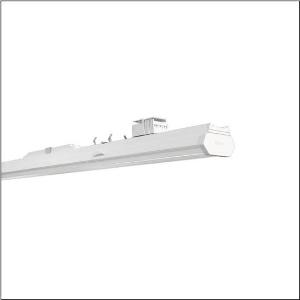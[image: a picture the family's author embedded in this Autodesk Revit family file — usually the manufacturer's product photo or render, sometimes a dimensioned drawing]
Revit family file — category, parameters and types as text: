
# Revit family: licross_r__21_protected_ho_52td13mn4fxs_5700
name_source: partatom
category: Lighting Fixtures
units: mm (PartAtom-declared; Revit-internal decimal feet)

## family parameters
Cut with Voids When Loaded = No
Host = Face
Light Source = No
Part Type = Normal
Room Calculation Point = No
Round Connector Dimension = Use Diameter
Shared = No

## types (1)
- --- (1 x LED, 15060 lm, 83.2 W, 4000K)
    Apparent Load = 83 VA
    CIE Flux Codes = 89 96 99 100 99
    Color Rendering = 80
    Color Temperature = 4000K
    Default Elevation = 1800 mm
    Description = Licross® 21 Protected HO, luminaire insert, of sheet steel, galvanised, coil coated, white, length: 1.500mm, width: 66mm, height: 67mm, LED rated luminous flux: 15.060lm, light colour: 840, control gear: ON/OFF Multilumen, with plug, 3-pole, with phase selection, mains connection: 220..240V, AC, 50/60Hz, rated input power: 83W, halogen-free wiring, primary light control with lens, of plastic, primary optical cover: cover, of PMMA, light emission: direct distribution, primary light characteristic: symmetric, protection rating (complete): IP54, insulation class (complete): insulation class I (protective earthing), certification: CE, ENEC, VDE, UKCA, protection symbol: D if used in an environment with non-conductive dust loads with corresponding accessories, impact resistance: IK06, permissible ambient temperature for indoor applications: -35..+35°C, corresponds to IFS (International Featured Standards) requirements for safety and quality in the food industry, reducing of maximum allowable ambient temperature of 5°C with ceiling mounting, LABS conformity tested according to VDMA 24364:2018-05, packaging unit: 1 piece
    Height = 92 mm
    Lamp = 1 x LED
    Lamp Light Flux = 15060 lm
    Lamp Power = 83.2 W
    Lamp count = 1
    Length = 1500 mm
    Luminous efficacy = 181 lm/W
    Manufacturer = Siteco
    ModVariant = No
    Model = 52TD13MN4FXS
    Mounting Place = Ceiling
    Mounting Type = Pendant
    Number of Poles = 1
    OnlyDefault = Yes
    Power Factor = 1
    Product Name = Licross® 21 Protected HO
    Product group = luminaire insert
    ProductGroupID = 901
    Protection Class = Protection class I
    Protection Degree = IP 54
    RLX_Detail_Level = 1
    RLX_Emergency_Light_Flux = 0 lm
    RLX_Emergency_Type = 0
    RLX_Emergency_Type_DB = No
    RlxData = <blob elided: 21993 chars, md5=baf12fe6>
    Socket = socket
    Standby Power = 0 W
    System Light Flux = 15060 lm
    System Power = 83 W
    Type Comments = factory setting: luminous flux: 100 % | (A | C | E) | 195 mA
    Type Image = l_1256148.jpg
    URL = http://relux.com
    VarID = @adj_077893
    Voltage = 0 V
    Weight = 0.00 kg
    Width = 88 mm

## geometry (parser evidence)
native form markers: Blend x4, Sweep x10
no freeform markers — native parametric forms only
